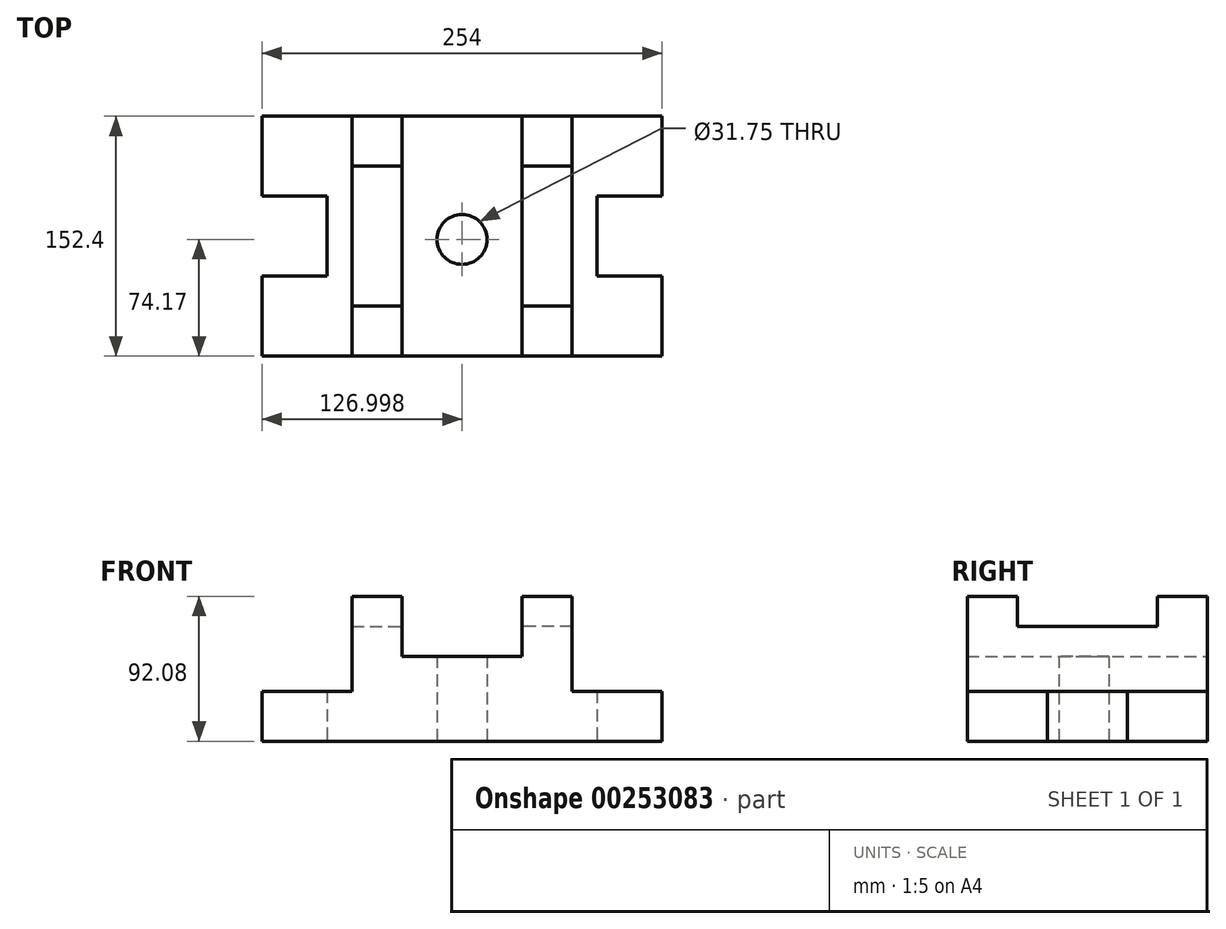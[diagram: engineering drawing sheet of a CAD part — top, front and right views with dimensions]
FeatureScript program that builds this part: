
annotation { "Feature Type Name" : "Feature", "Feature Type Description" : "" }
export const myFeature = defineFeature(function(context is Context, id is Id, definition is map)
    precondition{}
    {
        {
            var Q0;
            Q0=qCreatedBy(makeId("Top.planeOp"),FACE);
            var sketch = newSketch(context, id + "F0", { "sketchPlane" : qUnion([Q0])});
            skLineSegment(sketch, "E0", {"start": v(-128.95, 78.23) * mm, "end": v(-71.8, 78.23) * mm});
            skLineSegment(sketch, "E1", {"start": v(125.05, 78.23) * mm, "end": v(125.05, 27.43) * mm});
            skLineSegment(sketch, "E2", {"start": v(-128.95, 78.23) * mm, "end": v(-128.95, 27.43) * mm});
            skLineSegment(sketch, "E3", {"start": v(-128.95, -74.17) * mm, "end": v(-71.8, -74.17) * mm});
            skLineSegment(sketch, "E4", {"start": v(125.05, 27.43) * mm, "end": v(83.77, 27.43) * mm});
            skLineSegment(sketch, "E5", {"start": v(83.77, 27.43) * mm, "end": v(83.77, -23.37) * mm});
            skLineSegment(sketch, "E6", {"start": v(125.05, -23.37) * mm, "end": v(83.77, -23.37) * mm});
            skLineSegment(sketch, "E7.trimOffspring", {"start": v(125.05, -23.37) * mm, "end": v(125.05, -74.17) * mm});
            skLineSegment(sketch, "E8", {"start": v(-128.95, 27.43) * mm, "end": v(-87.68, 27.43) * mm});
            skLineSegment(sketch, "E9", {"start": v(-87.68, 27.43) * mm, "end": v(-87.68, -23.37) * mm});
            skLineSegment(sketch, "E10", {"start": v(-87.68, -23.37) * mm, "end": v(-128.95, -23.37) * mm});
            skLineSegment(sketch, "E11.trimOffspring", {"start": v(-128.95, -23.37) * mm, "end": v(-128.95, -74.17) * mm});
            skLineSegment(sketch, "E12.trimOffspring", {"start": v(67.9, 78.23) * mm, "end": v(125.05, 78.23) * mm});
            skLineSegment(sketch, "E13.trimOffspring", {"start": v(67.9, -74.17) * mm, "end": v(125.05, -74.17) * mm});
            skLineSegment(sketch, "E14", {"start": v(-71.8, 78.23) * mm, "end": v(-40.05, 78.23) * mm});
            skLineSegment(sketch, "E15", {"start": v(-71.8, -74.17) * mm, "end": v(-40.05, -74.17) * mm});
            skLineSegment(sketch, "E16", {"start": v(-40.05, -74.17) * mm, "end": v(-40.05, 78.23) * mm});
            skLineSegment(sketch, "E17", {"start": v(67.9, 78.23) * mm, "end": v(36.15, 78.23) * mm});
            skLineSegment(sketch, "E18", {"start": v(36.15, 78.23) * mm, "end": v(36.15, 0) * mm});
            skLineSegment(sketch, "E19", {"start": v(36.15, -74.17) * mm, "end": v(67.9, -74.17) * mm});
            skLineSegment(sketch, "E20", {"start": v(-1.95, -74.17) * mm, "end": v(36.15, -74.17) * mm});
            skLineSegment(sketch, "E21", {"start": v(-1.95, 78.23) * mm, "end": v(36.15, 78.23) * mm});
            skLineSegment(sketch, "E22", {"start": v(36.15, -74.17) * mm, "end": v(36.15, 0) * mm});
            skCircle(sketch, "E23", {"center": v(-1.95, 0) * mm, "radius": 15.88 * mm});
            skPoint(sketch, "E24.start.orphan", {"position": v(-40.05, 0) * mm});
            skLineSegment(sketch, "E25", {"start": v(-40.05, 78.23) * mm, "end": v(-1.95, 78.23) * mm});
            skLineSegment(sketch, "E26", {"start": v(-1.95, -74.17) * mm, "end": v(-40.05, -74.17) * mm});
            skLineSegment(sketch, "E27", {"start": v(67.9, 78.23) * mm, "end": v(67.9, 46.48) * mm});
            skLineSegment(sketch, "E28", {"start": v(67.9, 46.48) * mm, "end": v(36.15, 46.48) * mm});
            skLineSegment(sketch, "E29", {"start": v(67.9, -74.17) * mm, "end": v(67.9, -42.42) * mm});
            skLineSegment(sketch, "E30", {"start": v(67.9, -42.42) * mm, "end": v(36.15, -42.42) * mm});
            skLineSegment(sketch, "E31", {"start": v(67.9, 46.48) * mm, "end": v(67.9, -42.42) * mm});
            skLineSegment(sketch, "E32", {"start": v(-71.8, 78.23) * mm, "end": v(-71.8, 46.48) * mm});
            skLineSegment(sketch, "E33", {"start": v(-71.8, 46.48) * mm, "end": v(-40.05, 46.48) * mm});
            skLineSegment(sketch, "E34", {"start": v(-71.8, -74.17) * mm, "end": v(-71.8, -42.42) * mm});
            skLineSegment(sketch, "E35", {"start": v(-71.8, -42.42) * mm, "end": v(-40.05, -42.42) * mm});
            skLineSegment(sketch, "E36", {"start": v(-71.8, 46.48) * mm, "end": v(-71.8, -42.42) * mm});
            skSolve(sketch);
        }
        {
            var Q0;
            Q0=makeQuery(id+"F0.imprint","IMPRINT",FACE,{"disambiguationData":[TD([[makeQuery(id+"F0.imprint","IMPRINT",EDGE,{"derivedFrom":sQuery(id+"F0.wireOp",EDGE,"E0")}),-1.0]])]});
            extrude(context, id + "F1", {"entities" : qUnion([Q0]), "depth" : 31.75 * mm});
        }
        {
            var Q0;
            Q0=makeQuery(id+"F0.imprint","IMPRINT",FACE,{"disambiguationData":[TD([[makeQuery(id+"F0.imprint","IMPRINT",EDGE,{"derivedFrom":sQuery(id+"F0.wireOp",EDGE,"E1")}),-1.0]])]});
            extrude(context, id + "F2", {"entities" : qUnion([Q0]), "operationType" : NewBodyOperationType.ADD, "depth" : 31.75 * mm});
        }
        {
            var Q0;
            {var subQ0=sQuery(id+"F0.wireOp",EDGE,"E15");Q0=makeQuery(id+"F0.imprint","IMPRINT",FACE,{"disambiguationData":[TD([[makeQuery(id+"F0.imprint","IMPRINT",EDGE,{"derivedFrom":subQ0}),1.0]])]});}
            extrude(context, id + "F3", {"entities" : qUnion([Q0]), "operationType" : NewBodyOperationType.ADD, "depth" : 92.07 * mm});
        }
        {
            var Q0;
            {var subQ0=sQuery(id+"F0.wireOp",EDGE,"E14");Q0=makeQuery(id+"F0.imprint","IMPRINT",FACE,{"disambiguationData":[TD([[makeQuery(id+"F0.imprint","IMPRINT",EDGE,{"derivedFrom":subQ0}),-1.0]])]});}
            var Q1;
            {var subQ0=sQuery(id+"F0.wireOp",EDGE,"E17");Q1=makeQuery(id+"F0.imprint","IMPRINT",FACE,{"disambiguationData":[TD([[makeQuery(id+"F0.imprint","IMPRINT",EDGE,{"derivedFrom":subQ0}),1.0]])]});}
            var Q2;
            {var subQ0=sQuery(id+"F0.wireOp",EDGE,"E19");Q2=makeQuery(id+"F0.imprint","IMPRINT",FACE,{"disambiguationData":[TD([[makeQuery(id+"F0.imprint","IMPRINT",EDGE,{"derivedFrom":subQ0}),1.0]])]});}
            extrude(context, id + "F4", {"entities" : qUnion([Q0, Q1, Q2]), "operationType" : NewBodyOperationType.ADD, "depth" : 92.07 * mm});
        }
        {
            var Q0;
            {var subQ4=sQuery(id+"F0.wireOp",EDGE,"E20");Q0=makeQuery(id+"F0.imprint","IMPRINT",FACE,{"disambiguationData":[TD([[makeQuery(id+"F0.imprint","IMPRINT",EDGE,{"derivedFrom":subQ4}),1.0]])]});}
            extrude(context, id + "F5", {"entities" : qUnion([Q0]), "depth" : 53.97 * mm});
        }
        {
            var Q0;
            {var subQ0=sQuery(id+"F0.wireOp",EDGE,"E33");Q0=makeQuery(id+"F0.imprint","IMPRINT",FACE,{"disambiguationData":[TD([[makeQuery(id+"F0.imprint","IMPRINT",EDGE,{"derivedFrom":subQ0}),-1.0]])]});}
            var Q1;
            {var subQ1=sQuery(id+"F0.wireOp",EDGE,"E28");Q1=makeQuery(id+"F0.imprint","IMPRINT",FACE,{"disambiguationData":[TD([[makeQuery(id+"F0.imprint","IMPRINT",EDGE,{"derivedFrom":subQ1}),1.0]])]});}
            extrude(context, id + "F6", {"entities" : qUnion([Q0, Q1]), "operationType" : NewBodyOperationType.ADD, "depth" : 73.02 * mm});
        }
    });
